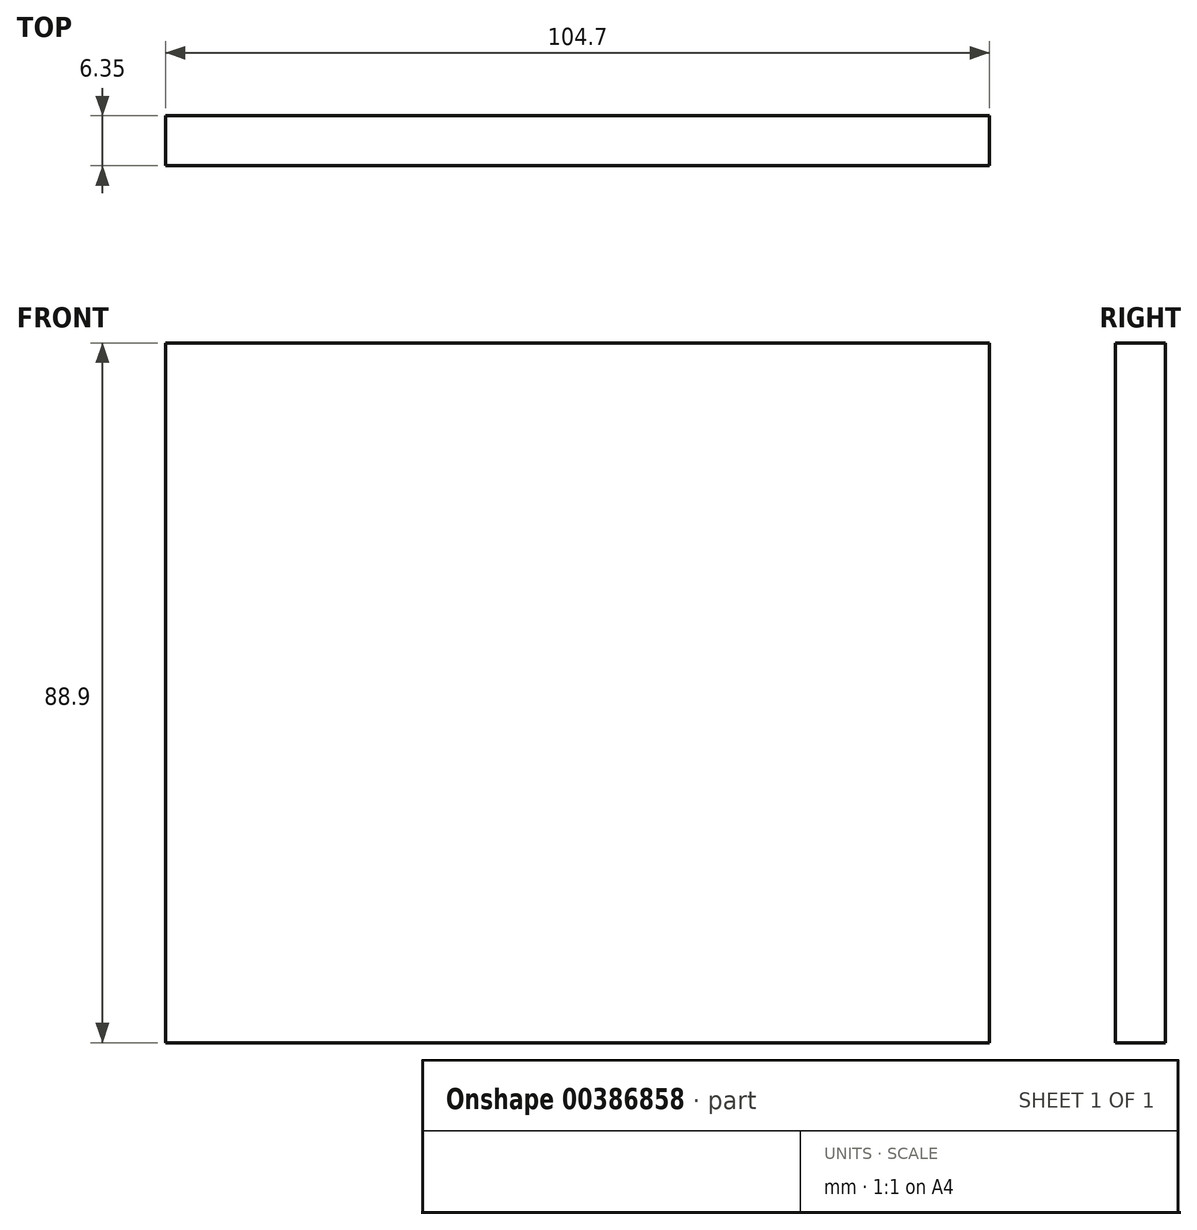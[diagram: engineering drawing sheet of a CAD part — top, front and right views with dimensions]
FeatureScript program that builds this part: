
annotation { "Feature Type Name" : "Feature", "Feature Type Description" : "" }
export const myFeature = defineFeature(function(context is Context, id is Id, definition is map)
    precondition{}
    {
        {
            var Q0;
            Q0=qCreatedBy(makeId("Front.planeOp"),FACE);
            var sketch = newSketch(context, id + "F0", { "sketchPlane" : qUnion([Q0])});
            skLineSegment(sketch, "E0.bottom", {"start": v(-52.35, 44.45) * mm, "end": v(52.35, 44.45) * mm});
            skLineSegment(sketch, "E0.top", {"start": v(-52.35, -44.45) * mm, "end": v(52.35, -44.45) * mm});
            skLineSegment(sketch, "E0.left", {"start": v(-52.35, 44.45) * mm, "end": v(-52.35, -44.45) * mm});
            skLineSegment(sketch, "E0.right", {"start": v(52.35, 44.45) * mm, "end": v(52.35, -44.45) * mm});
            skPoint(sketch, "E0.middle", {"position": v(0, 0) * mm});
            skSolve(sketch);
        }
        {
            var Q0;
            Q0 = qSketchRegion(id + "F0", true);
            extrude(context, id + "F1", {"entities" : qUnion([Q0]), "depth" : 6.35 * mm, "offsetDistance" : 25.4 * mm});
        }
    });
